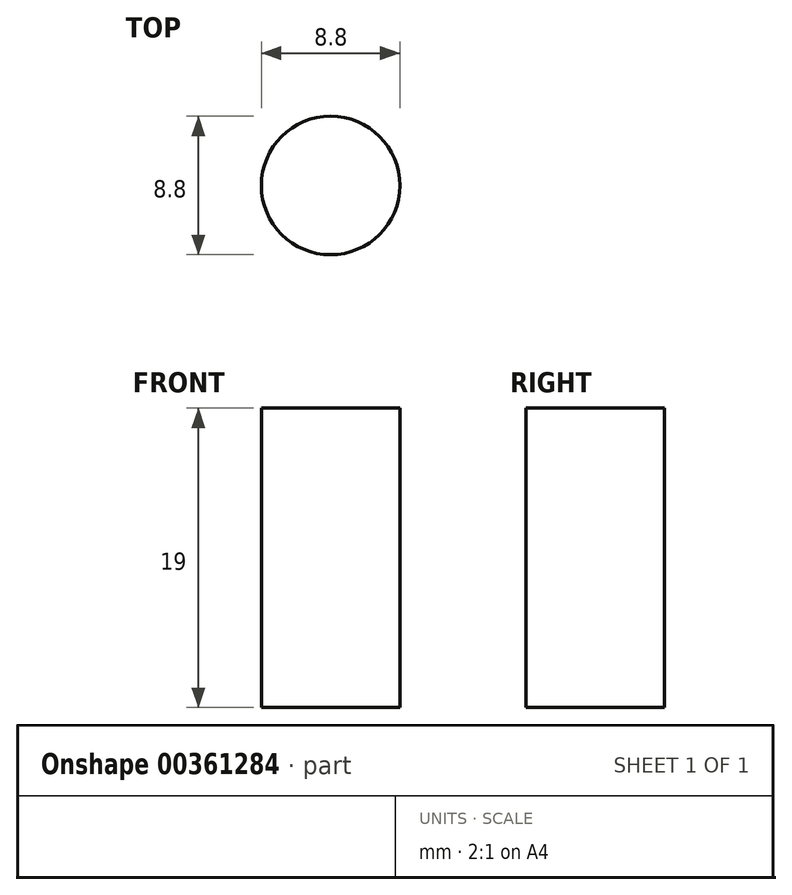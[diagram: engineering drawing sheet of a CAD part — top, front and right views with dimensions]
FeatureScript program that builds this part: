
annotation { "Feature Type Name" : "Feature", "Feature Type Description" : "" }
export const myFeature = defineFeature(function(context is Context, id is Id, definition is map)
    precondition{}
    {
        {
            var Q0;
            Q0=qCreatedBy(makeId("Top.planeOp"),FACE);
            var sketch = newSketch(context, id + "F0", { "sketchPlane" : qUnion([Q0])});
            skCircle(sketch, "E0", {"center": v(0, 0) * mm, "radius": 4.4 * mm});
            skSolve(sketch);
        }
        {
            var Q0;
            Q0 = qSketchRegion(id + "F0", true);
            extrude(context, id + "F1", {"entities" : qUnion([Q0]), "depth" : 19 * mm});
        }
    });
